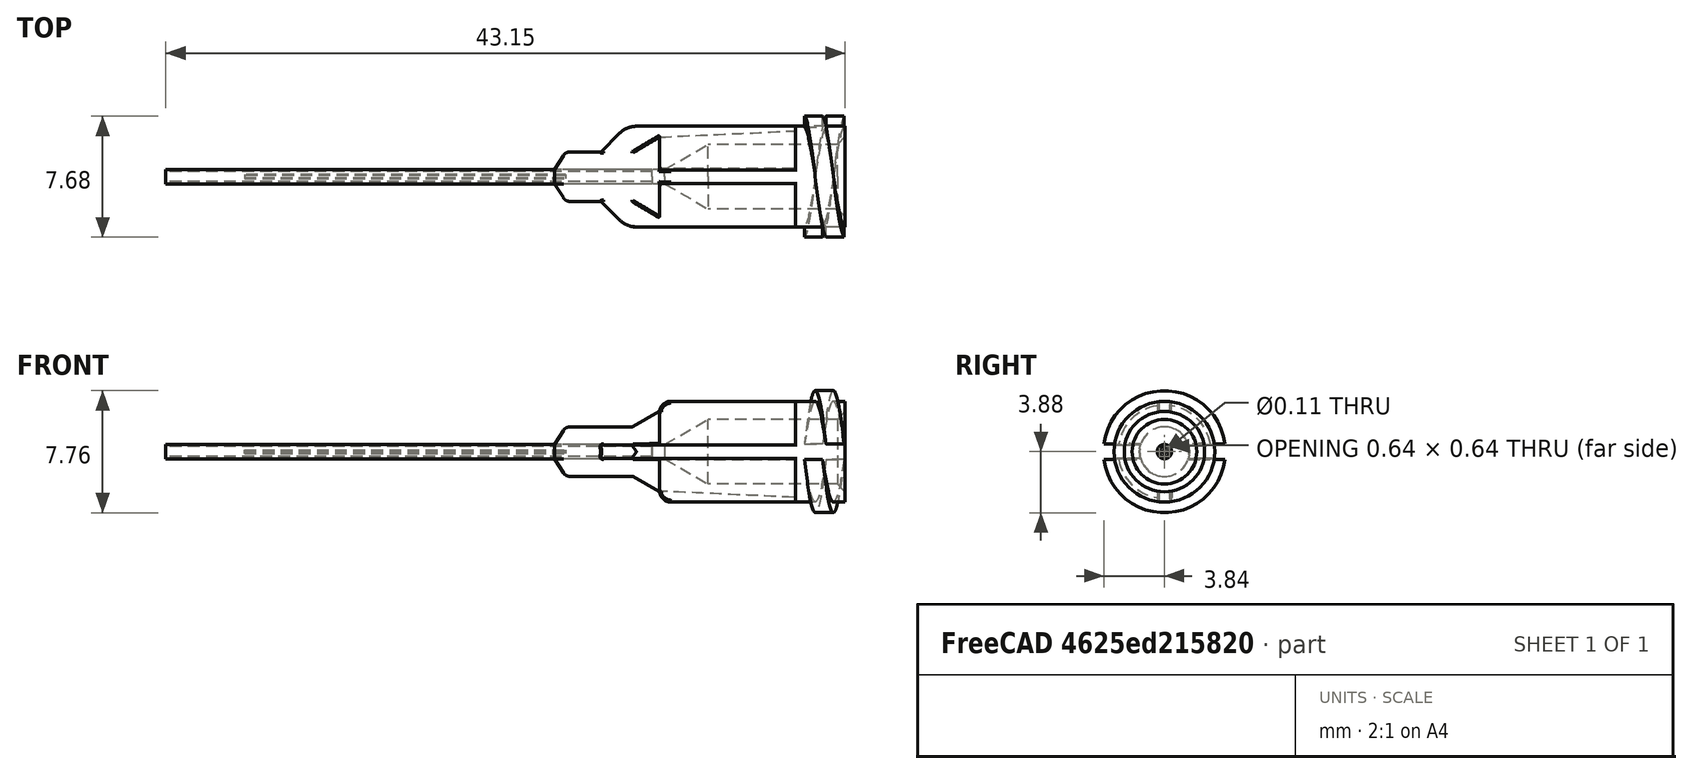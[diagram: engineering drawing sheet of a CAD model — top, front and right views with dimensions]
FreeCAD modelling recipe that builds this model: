
FCSTD DOCUMENT  (FreeCAD 0.19R24344 (Git))
Label: Luer-Tether
License: All rights reserved
LicenseURL: http://en.wikipedia.org/wiki/All_rights_reserved
objects: Part::Feature×2, PartDesign::CoordinateSystem×2, Sketcher::SketchObject×1, PartDesign::Pad×1, PartDesign::Body×1, Part::Compound2×1, Part::FeaturePython×1, App::Part×1
note: 9 computed .brp shape members not serialized (recipe doc carries the construction recipe); baked Part::Feature solids carry a one-line shape summary decoded from their .brp

FEATURE [Part::Feature] Solid
  shape: bbox 18.46 x 7.75 x 8.149 mm, 114 faces (baked)
FEATURE [Sketcher::SketchObject] Sketch
  FullyConstrained = true
  MapMode = 5
  Placement = pos=(0,0,0) rot=(0.57735,0.57735,0.57735;2.0944rad)
  Support = -> [YZ_Plane]
  sketch-geometry (2):
    g0: Circle CenterX=0 CenterY=0 CenterZ=0 NormalX=0 NormalY=0 NormalZ=1 AngleXU=0 Radius=0.1175
    g1: Circle CenterX=0 CenterY=0 CenterZ=0 NormalX=0 NormalY=0 NormalZ=1 AngleXU=0 Radius=0.054
  constraints (4):
    c: Diameter(g0) = 0.235
    c: Diameter(g1) = 0.108
    c: Coincident(g0,g-1)
    c: Coincident(g1,g0)
FEATURE [PartDesign::Pad] Pad
  Direction = (1,1,1)
  Length = 20.4
  Length2 = 100
  Placement = pos=(0,0,0) rot=(0.57735,0.57735,0.57735;2.0944rad)
  Profile = -> Sketch
  Reversed = true
  Type = 0
FEATURE [PartDesign::Body] Body
  Group = -> [Sketch,Pad]
  Origin = -> Origin
  Tip = -> Pad
FEATURE [PartDesign::CoordinateSystem] LCS_0
  AttacherType = Attacher::AttachEngine3D
  MapMode = 2
  Support = -> [X_Axis001]
FEATURE [Part::Feature] Solid001
  shape: bbox 30.9 x 0.91 x 0.91 mm, 6 faces (baked)
FEATURE [Part::Compound2] Compound  label="Syringe Tip"
  Links = -> [Solid,Solid001]
FEATURE [Part::FeaturePython] Compound_child0  label="Luer"  # WARN: FeaturePython — macro-defined, semantics opaque (R4)
  Base = -> Compound
  FilterType = 1
  Invert = false
  OverrideMaxVal = 0
  WindowFrom = 80
  WindowTo = 100
  items = 0
FEATURE [PartDesign::CoordinateSystem] LCS_Luer
  AttacherType = Attacher::AttachEngine3D
  MapMode = 45
  Placement = pos=(17.75,-9e-16,1e-16) rot=(0.57735,0.57735,0.57735;2.0944rad)
  Support = -> [Compound_child0]
FEATURE [App::Part] Part
  Group = -> [LCS_0,Solid,Solid001,Compound,Body,Compound_child0,LCS_Luer]
  Origin = -> Origin001
